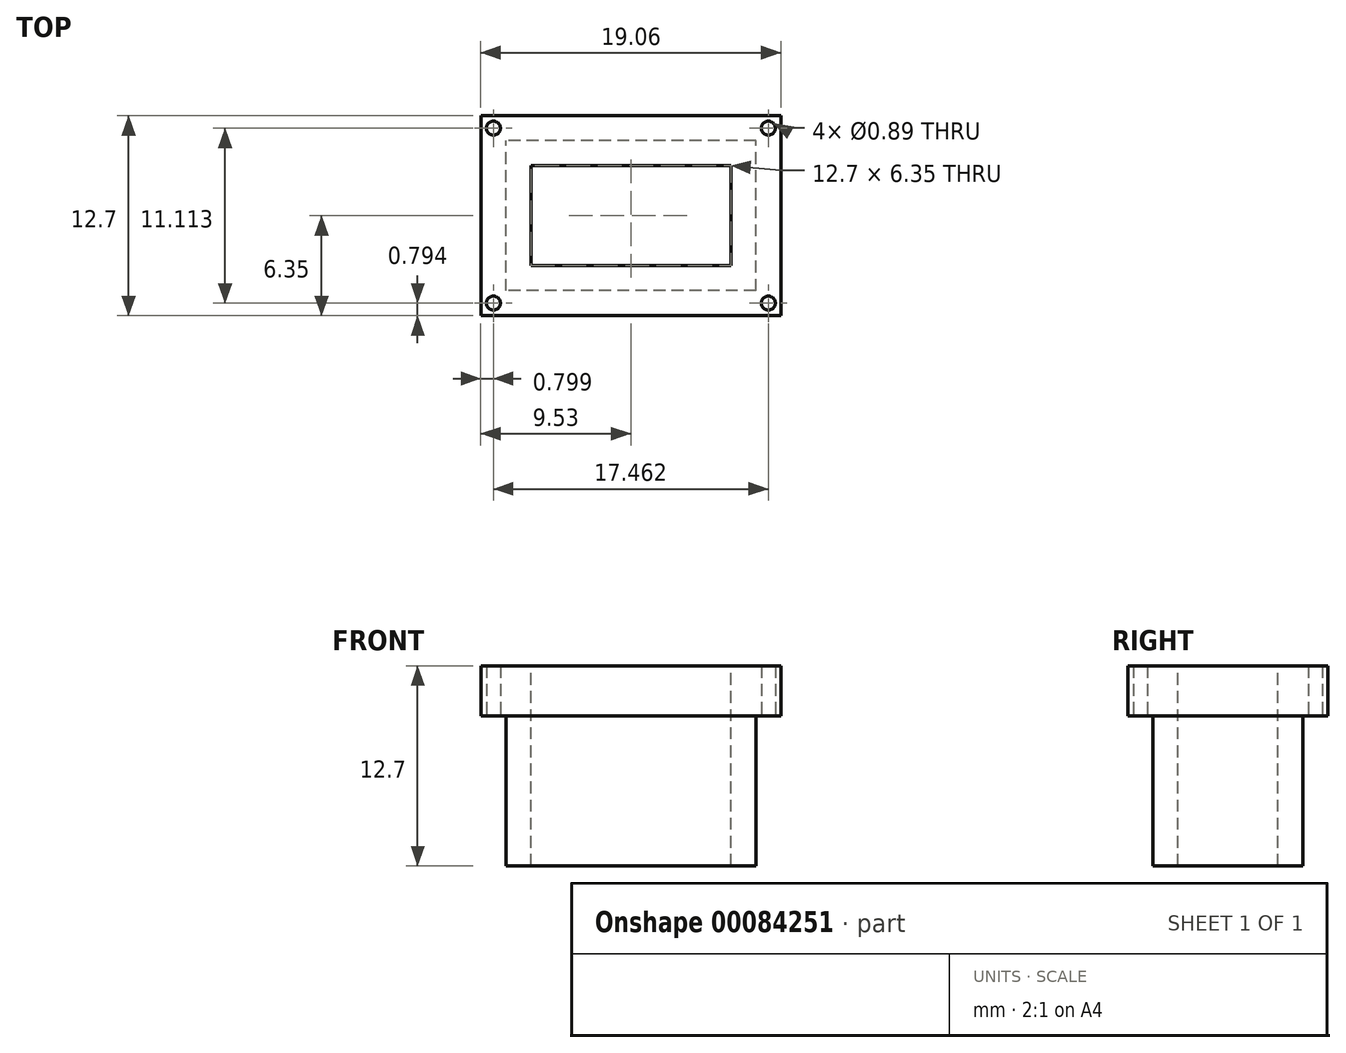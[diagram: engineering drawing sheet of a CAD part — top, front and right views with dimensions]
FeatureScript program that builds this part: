
annotation { "Feature Type Name" : "Feature", "Feature Type Description" : "" }
export const myFeature = defineFeature(function(context is Context, id is Id, definition is map)
    precondition{}
    {
        {
            var Q0;
            Q0=qCreatedBy(makeId("Top.planeOp"),FACE);
            var sketch = newSketch(context, id + "F0", { "sketchPlane" : qUnion([Q0])});
            skLineSegment(sketch, "E0.bottom", {"start": v(6.35, 3.18) * mm, "end": v(-6.35, 3.18) * mm});
            skLineSegment(sketch, "E0.top", {"start": v(6.35, -3.18) * mm, "end": v(-6.35, -3.17) * mm});
            skLineSegment(sketch, "E0.left", {"start": v(6.35, 3.17) * mm, "end": v(6.35, -3.17) * mm});
            skLineSegment(sketch, "E0.right", {"start": v(-6.35, 3.17) * mm, "end": v(-6.35, -3.17) * mm});
            skLineSegment(sketch, "E1.bottom", {"start": v(9.53, 6.35) * mm, "end": v(-9.52, 6.35) * mm});
            skLineSegment(sketch, "E1.top", {"start": v(9.53, -6.35) * mm, "end": v(-9.52, -6.35) * mm});
            skLineSegment(sketch, "E1.left", {"start": v(9.53, 6.35) * mm, "end": v(9.52, -6.35) * mm});
            skLineSegment(sketch, "E1.right", {"start": v(-9.52, 6.35) * mm, "end": v(-9.53, -6.35) * mm});
            skPoint(sketch, "E1.middle", {"position": v(0, 0) * mm});
            skLineSegment(sketch, "E2", {"start": v(0, -3.17) * mm, "end": v(0, 3.17) * mm});
            skLineSegment(sketch, "E3", {"start": v(0, -6.35) * mm, "end": v(0, 6.35) * mm});
            skLineSegment(sketch, "E4.bottom", {"start": v(7.94, -4.76) * mm, "end": v(-7.94, -4.76) * mm});
            skLineSegment(sketch, "E4.top", {"start": v(7.94, 4.76) * mm, "end": v(-7.94, 4.76) * mm});
            skLineSegment(sketch, "E4.left", {"start": v(7.94, -4.76) * mm, "end": v(7.94, 4.76) * mm});
            skLineSegment(sketch, "E4.right", {"start": v(-7.94, -4.76) * mm, "end": v(-7.94, 4.76) * mm});
            skLineSegment(sketch, "E5", {"start": v(-6.35, -3.17) * mm, "end": v(-9.52, -6.35) * mm});
            skSolve(sketch);
        }
        {
            var Q0;
            Q0 = qSketchRegion(id + "F0", true);
            var Q1;
            {var subQ1=sQuery(id+"F0.wireOp",EDGE,"E0.top");var subQ3=sQuery(id+"F0.wireOp",EDGE,"E3");var subQ4=makeQuery(id+"F0.imprint","INTERSECT",VERTEX,{"derivedFrom":[subQ1,subQ3]});Q1=makeQuery(id+"F0.imprint","IMPRINT",FACE,{"disambiguationData":[TD([[makeQuery(id+"F0.imprint","IMPRINT",EDGE,{"disambiguationData":[TD([[subQ4,1.0]])],"derivedFrom":subQ3}),1.0]])]});}
            var Q2;
            {var subQ6=sQuery(id+"F0.wireOp",EDGE,"E0.right");Q2=makeQuery(id+"F0.imprint","IMPRINT",FACE,{"disambiguationData":[TD([[makeQuery(id+"F0.imprint","IMPRINT",EDGE,{"derivedFrom":subQ6}),-1.0]])]});}
            var Q3;
            {var subQ6=sQuery(id+"F0.wireOp",EDGE,"E0.left");Q3=makeQuery(id+"F0.imprint","IMPRINT",FACE,{"disambiguationData":[TD([[makeQuery(id+"F0.imprint","IMPRINT",EDGE,{"derivedFrom":subQ6}),1.0]])]});}
            extrude(context, id + "F1", {"entities" : qUnion([Q0, Q1, Q2, Q3]), "oppositeDirection" : true, "depth" : 3.17 * mm});
        }
        {
            var Q0;
            {var subQ1=sQuery(id+"F0.wireOp",EDGE,"E0.top");var subQ3=sQuery(id+"F0.wireOp",EDGE,"E3");var subQ4=makeQuery(id+"F0.imprint","INTERSECT",VERTEX,{"derivedFrom":[subQ1,subQ3]});Q0=makeQuery(id+"F0.imprint","IMPRINT",FACE,{"disambiguationData":[TD([[makeQuery(id+"F0.imprint","IMPRINT",EDGE,{"disambiguationData":[TD([[subQ4,1.0]])],"derivedFrom":subQ3}),1.0]])]});}
            var Q1;
            {var subQ6=sQuery(id+"F0.wireOp",EDGE,"E0.left");Q1=makeQuery(id+"F0.imprint","IMPRINT",FACE,{"disambiguationData":[TD([[makeQuery(id+"F0.imprint","IMPRINT",EDGE,{"derivedFrom":subQ6}),1.0]])]});}
            var Q2;
            {var subQ6=sQuery(id+"F0.wireOp",EDGE,"E0.right");Q2=makeQuery(id+"F0.imprint","IMPRINT",FACE,{"disambiguationData":[TD([[makeQuery(id+"F0.imprint","IMPRINT",EDGE,{"derivedFrom":subQ6}),-1.0]])]});}
            extrude(context, id + "F2", {"entities" : qUnion([Q0, Q1, Q2]), "operationType" : NewBodyOperationType.ADD, "oppositeDirection" : true, "depth" : 12.7 * mm});
        }
        {
            var Q0;
            Q0=makeQuery(id+"F1.opExtrude","CAP_FACE",FACE,{"disambiguationData":[OSD([sQuery(id+"F0.wireOp",EDGE,"E0.bottom"),sQuery(id+"F0.wireOp",EDGE,"E0.top"),sQuery(id+"F0.wireOp",EDGE,"E0.left"),sQuery(id+"F0.wireOp",EDGE,"E0.right"),sQuery(id+"F0.wireOp",EDGE,"E1.bottom"),sQuery(id+"F0.wireOp",EDGE,"E1.top"),sQuery(id+"F0.wireOp",EDGE,"E1.left"),sQuery(id+"F0.wireOp",EDGE,"E1.right")])],"isStart":false});
            var sketch = newSketch(context, id + "F3", { "sketchPlane" : qUnion([Q0])});
            skLineSegment(sketch, "E6.0", {"start": v(-7.94, 4.76) * mm, "end": v(-7.94, -4.76) * mm});
            skLineSegment(sketch, "E6.1", {"start": v(7.94, 4.76) * mm, "end": v(-7.94, 4.76) * mm});
            skLineSegment(sketch, "E6.2", {"start": v(9.52, 6.35) * mm, "end": v(-9.52, 6.35) * mm});
            skLineSegment(sketch, "E6.3", {"start": v(-9.52, -6.35) * mm, "end": v(-9.53, 6.35) * mm});
            skLineSegment(sketch, "E6.4", {"start": v(7.94, 4.76) * mm, "end": v(7.94, -4.76) * mm});
            skLineSegment(sketch, "E6.5", {"start": v(9.53, -6.35) * mm, "end": v(9.52, 6.35) * mm});
            skLineSegment(sketch, "E6.6", {"start": v(7.94, -4.76) * mm, "end": v(-7.94, -4.76) * mm});
            skLineSegment(sketch, "E6.7", {"start": v(9.53, -6.35) * mm, "end": v(-9.52, -6.35) * mm});
            skLineSegment(sketch, "E7.bottom", {"start": v(-7.94, 4.76) * mm, "end": v(-9.52, 4.76) * mm});
            skLineSegment(sketch, "E7.top", {"start": v(-7.94, 6.35) * mm, "end": v(-9.52, 6.35) * mm});
            skLineSegment(sketch, "E7.left", {"start": v(-7.94, 4.76) * mm, "end": v(-7.94, 6.35) * mm});
            skLineSegment(sketch, "E7.right", {"start": v(-9.52, 4.76) * mm, "end": v(-9.52, 6.35) * mm});
            skLineSegment(sketch, "E8.bottom", {"start": v(7.94, 4.76) * mm, "end": v(9.52, 4.76) * mm});
            skLineSegment(sketch, "E8.top", {"start": v(7.94, 6.35) * mm, "end": v(9.52, 6.35) * mm});
            skLineSegment(sketch, "E8.left", {"start": v(7.94, 4.76) * mm, "end": v(7.94, 6.35) * mm});
            skLineSegment(sketch, "E8.right", {"start": v(9.52, 4.76) * mm, "end": v(9.52, 6.35) * mm});
            skLineSegment(sketch, "E9.bottom", {"start": v(9.53, -6.35) * mm, "end": v(7.94, -6.35) * mm});
            skLineSegment(sketch, "E9.top", {"start": v(9.53, -4.76) * mm, "end": v(7.94, -4.76) * mm});
            skLineSegment(sketch, "E9.left", {"start": v(9.53, -6.35) * mm, "end": v(9.53, -4.76) * mm});
            skLineSegment(sketch, "E9.right", {"start": v(7.94, -6.35) * mm, "end": v(7.94, -4.76) * mm});
            skLineSegment(sketch, "E10.bottom", {"start": v(-7.94, -4.76) * mm, "end": v(-9.52, -4.76) * mm});
            skLineSegment(sketch, "E10.top", {"start": v(-7.94, -6.35) * mm, "end": v(-9.52, -6.35) * mm});
            skLineSegment(sketch, "E10.left", {"start": v(-7.94, -4.76) * mm, "end": v(-7.94, -6.35) * mm});
            skLineSegment(sketch, "E10.right", {"start": v(-9.52, -4.76) * mm, "end": v(-9.52, -6.35) * mm});
            skCircle(sketch, "E11", {"center": v(-8.73, 5.56) * mm, "radius": 0.44 * mm});
            skPoint(sketch, "E11.centerSnap0", {"position": v(-9.52, 5.56) * mm});
            skPoint(sketch, "E11.centerSnap1", {"position": v(-8.73, 4.76) * mm});
            skCircle(sketch, "E12", {"center": v(8.73, 5.56) * mm, "radius": 0.44 * mm});
            skPoint(sketch, "E12.centerSnap0", {"position": v(8.73, 4.76) * mm});
            skPoint(sketch, "E12.centerSnap1", {"position": v(7.94, 5.56) * mm});
            skCircle(sketch, "E13", {"center": v(8.73, -5.56) * mm, "radius": 0.44 * mm});
            skPoint(sketch, "E13.centerSnap0", {"position": v(7.94, -5.56) * mm});
            skPoint(sketch, "E13.centerSnap1", {"position": v(8.73, -6.35) * mm});
            skCircle(sketch, "E14", {"center": v(-8.73, -5.56) * mm, "radius": 0.44 * mm});
            skPoint(sketch, "E14.centerSnap0", {"position": v(-9.52, -5.56) * mm});
            skPoint(sketch, "E14.centerSnap1", {"position": v(-8.73, -6.35) * mm});
            skSolve(sketch);
        }
        {
            var Q0;
            Q0=makeQuery(id+"F3.imprint","IMPRINT",FACE,{"disambiguationData":[TD([[makeQuery(id+"F3.imprint","IMPRINT",EDGE,{"derivedFrom":sQuery(id+"F3.wireOp",EDGE,"E11")}),1.0]])]});
            var Q1;
            Q1=makeQuery(id+"F3.imprint","IMPRINT",FACE,{"disambiguationData":[TD([[makeQuery(id+"F3.imprint","IMPRINT",EDGE,{"derivedFrom":sQuery(id+"F3.wireOp",EDGE,"E12")}),1.0]])]});
            var Q2;
            Q2=makeQuery(id+"F3.imprint","IMPRINT",FACE,{"disambiguationData":[TD([[makeQuery(id+"F3.imprint","IMPRINT",EDGE,{"derivedFrom":sQuery(id+"F3.wireOp",EDGE,"E13")}),1.0]])]});
            var Q3;
            Q3=makeQuery(id+"F3.imprint","IMPRINT",FACE,{"disambiguationData":[TD([[makeQuery(id+"F3.imprint","IMPRINT",EDGE,{"derivedFrom":sQuery(id+"F3.wireOp",EDGE,"E14")}),1.0]])]});
            extrude(context, id + "F4", {"entities" : qUnion([Q0, Q1, Q2, Q3]), "operationType" : NewBodyOperationType.REMOVE, "oppositeDirection" : true, "depth" : 25.4 * mm});
        }
    });
